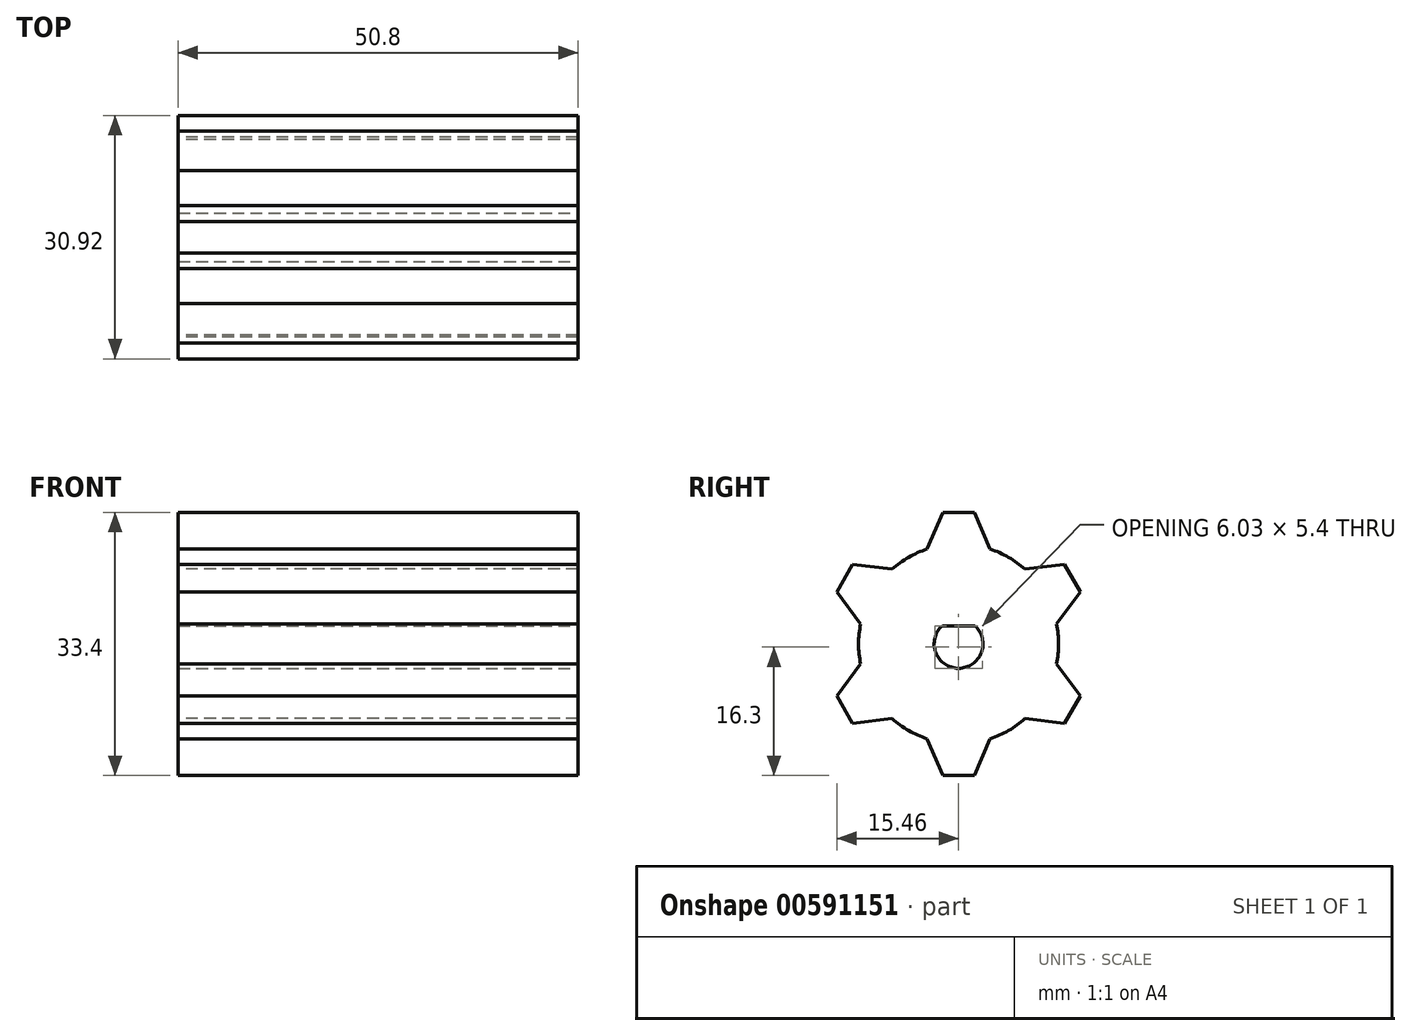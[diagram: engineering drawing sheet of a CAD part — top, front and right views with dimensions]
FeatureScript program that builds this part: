
annotation { "Feature Type Name" : "Feature", "Feature Type Description" : "" }
export const myFeature = defineFeature(function(context is Context, id is Id, definition is map)
    precondition{}
    {
        {
            var Q0;
            Q0=qCreatedBy(makeId("Right.planeOp"),FACE);
            var sketch = newSketch(context, id + "F0", { "sketchPlane" : qUnion([Q0])});
            skCircle(sketch, "E0", {"center": v(0, 0) * mm, "radius": 12.7 * mm});
            skLineSegment(sketch, "E1", {"start": v(0, 0) * mm, "end": v(0, 12.7) * mm, "construction": true});
            skLineSegment(sketch, "E2", {"start": v(0, 16.7) * mm, "end": v(-2, 16.7) * mm});
            skLineSegment(sketch, "E3", {"start": v(-2, 16.7) * mm, "end": v(-4, 12.05) * mm});
            skLineSegment(sketch, "E4.MirrorCS", {"start": v(0, 16.7) * mm, "end": v(2, 16.7) * mm});
            skLineSegment(sketch, "E5.MirrorCS", {"start": v(2, 16.7) * mm, "end": v(4, 12.05) * mm});
            skLineSegment(sketch, "E6.1.0", {"start": v(-15.46, 6.62) * mm, "end": v(-12.44, 2.56) * mm});
            skLineSegment(sketch, "E6.1.1", {"start": v(-14.46, 8.35) * mm, "end": v(-15.46, 6.62) * mm});
            skLineSegment(sketch, "E6.1.2", {"start": v(-14.46, 8.35) * mm, "end": v(-13.46, 10.08) * mm});
            skLineSegment(sketch, "E6.1.3", {"start": v(-13.46, 10.08) * mm, "end": v(-8.44, 9.5) * mm});
            skLineSegment(sketch, "E6.2.0", {"start": v(-13.46, -10.08) * mm, "end": v(-8.44, -9.5) * mm});
            skLineSegment(sketch, "E6.2.1", {"start": v(-14.46, -8.35) * mm, "end": v(-13.46, -10.08) * mm});
            skLineSegment(sketch, "E6.2.2", {"start": v(-14.46, -8.35) * mm, "end": v(-15.46, -6.62) * mm});
            skLineSegment(sketch, "E6.2.3", {"start": v(-15.46, -6.62) * mm, "end": v(-12.44, -2.56) * mm});
            skLineSegment(sketch, "E6.3.0", {"start": v(2, -16.7) * mm, "end": v(4, -12.05) * mm});
            skLineSegment(sketch, "E6.3.1", {"start": v(0, -16.7) * mm, "end": v(2, -16.7) * mm});
            skLineSegment(sketch, "E6.3.2", {"start": v(0, -16.7) * mm, "end": v(-2, -16.7) * mm});
            skLineSegment(sketch, "E6.3.3", {"start": v(-2, -16.7) * mm, "end": v(-4, -12.05) * mm});
            skLineSegment(sketch, "E6.4.0", {"start": v(15.46, -6.62) * mm, "end": v(12.44, -2.56) * mm});
            skLineSegment(sketch, "E6.4.1", {"start": v(14.46, -8.35) * mm, "end": v(15.46, -6.62) * mm});
            skLineSegment(sketch, "E6.4.2", {"start": v(14.46, -8.35) * mm, "end": v(13.46, -10.08) * mm});
            skLineSegment(sketch, "E6.4.3", {"start": v(13.46, -10.08) * mm, "end": v(8.44, -9.5) * mm});
            skLineSegment(sketch, "E6.5.0", {"start": v(13.46, 10.08) * mm, "end": v(8.44, 9.5) * mm});
            skLineSegment(sketch, "E6.5.1", {"start": v(14.46, 8.35) * mm, "end": v(13.46, 10.08) * mm});
            skLineSegment(sketch, "E6.5.2", {"start": v(14.46, 8.35) * mm, "end": v(15.46, 6.62) * mm});
            skLineSegment(sketch, "E6.5.3", {"start": v(15.46, 6.62) * mm, "end": v(12.44, 2.56) * mm});
            skSolve(sketch);
        }
        {
            var Q0;
            Q0 = qSketchRegion(id + "F0", true);
            extrude(context, id + "F1", {"entities" : qUnion([Q0]), "depth" : 50.8 * mm, "offsetDistance" : 25.4 * mm});
        }
        {
            var Q0;
            Q0=makeQuery(id+"F1.opExtrude","CAP_FACE",FACE,{"disambiguationData":[OSD([sQuery(id+"F0.wireOp",EDGE,"E0"),sQuery(id+"F0.wireOp",EDGE,"E2"),sQuery(id+"F0.wireOp",EDGE,"E3"),sQuery(id+"F0.wireOp",EDGE,"E4.MirrorCS"),sQuery(id+"F0.wireOp",EDGE,"E5.MirrorCS"),sQuery(id+"F0.wireOp",EDGE,"E6.1.0"),sQuery(id+"F0.wireOp",EDGE,"E6.1.1"),sQuery(id+"F0.wireOp",EDGE,"E6.1.2"),sQuery(id+"F0.wireOp",EDGE,"E6.1.3"),sQuery(id+"F0.wireOp",EDGE,"E6.2.0"),sQuery(id+"F0.wireOp",EDGE,"E6.2.1"),sQuery(id+"F0.wireOp",EDGE,"E6.2.2"),sQuery(id+"F0.wireOp",EDGE,"E6.2.3"),sQuery(id+"F0.wireOp",EDGE,"E6.3.0"),sQuery(id+"F0.wireOp",EDGE,"E6.3.1"),sQuery(id+"F0.wireOp",EDGE,"E6.3.2"),sQuery(id+"F0.wireOp",EDGE,"E6.3.3"),sQuery(id+"F0.wireOp",EDGE,"E6.4.0"),sQuery(id+"F0.wireOp",EDGE,"E6.4.1"),sQuery(id+"F0.wireOp",EDGE,"E6.4.2"),sQuery(id+"F0.wireOp",EDGE,"E6.4.3"),sQuery(id+"F0.wireOp",EDGE,"E6.5.0"),sQuery(id+"F0.wireOp",EDGE,"E6.5.1"),sQuery(id+"F0.wireOp",EDGE,"E6.5.2"),sQuery(id+"F0.wireOp",EDGE,"E6.5.3")])],"isStart":false});
            var sketch = newSketch(context, id + "F2", { "sketchPlane" : qUnion([Q0])});
            skArc(sketch, "E7", {"start": v(-2.08, 2.3) * mm, "mid": v(0, -3.1) * mm, "end": v(2.08, 2.3) * mm});
            skLineSegment(sketch, "E8", {"start": v(-2.08, 2.3) * mm, "end": v(2.08, 2.3) * mm});
            skSolve(sketch);
        }
        {
            var Q0;
            Q0 = qSketchRegion(id + "F2", true);
            extrude(context, id + "F3", {"entities" : qUnion([Q0]), "operationType" : NewBodyOperationType.REMOVE, "oppositeDirection" : true, "depth" : 101.6 * mm, "offsetDistance" : 25.4 * mm});
        }
    });
